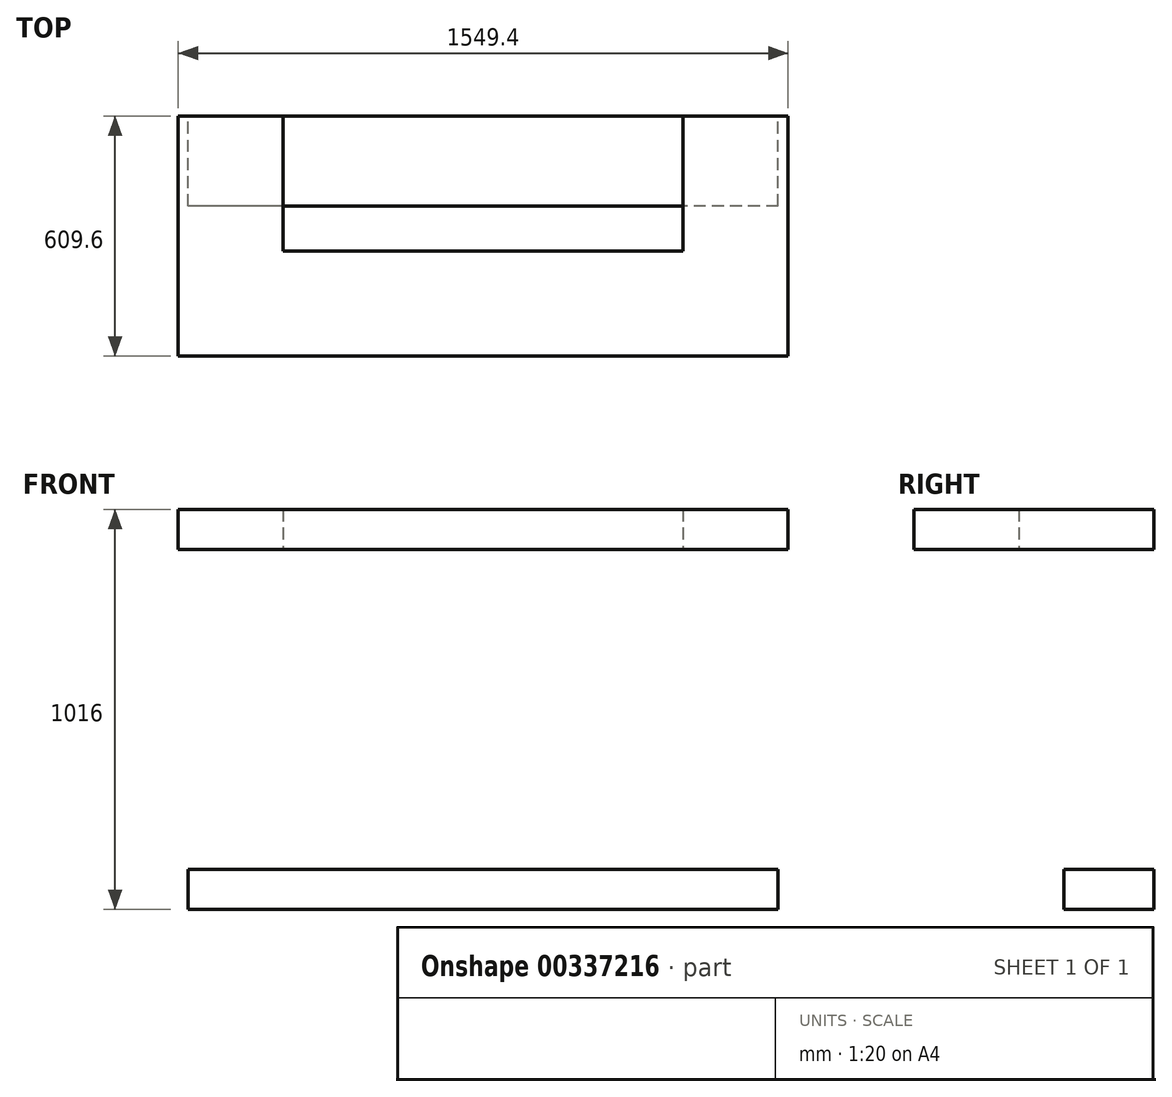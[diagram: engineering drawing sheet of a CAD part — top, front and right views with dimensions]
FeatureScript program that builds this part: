
annotation { "Feature Type Name" : "Feature", "Feature Type Description" : "" }
export const myFeature = defineFeature(function(context is Context, id is Id, definition is map)
    precondition{}
    {
        {
            var Q0;
            Q0=qCreatedBy(makeId("Top.planeOp"),FACE);
            var sketch = newSketch(context, id + "F0", { "sketchPlane" : qUnion([Q0])});
            skLineSegment(sketch, "E0", {"start": v(0, 0) * mm, "end": v(-749.3, 0) * mm, "construction": true});
            skLineSegment(sketch, "E1", {"start": v(-749.3, 0) * mm, "end": v(-749.3, -228.6) * mm, "construction": true});
            skLineSegment(sketch, "E2", {"start": v(-749.3, -228.6) * mm, "end": v(749.3, -228.6) * mm, "construction": true});
            skLineSegment(sketch, "E3.bottom", {"start": v(749.3, -228.6) * mm, "end": v(-749.3, -228.6) * mm});
            skLineSegment(sketch, "E3.top", {"start": v(749.3, 0) * mm, "end": v(-749.3, 0) * mm});
            skLineSegment(sketch, "E3.left", {"start": v(749.3, -228.6) * mm, "end": v(749.3, 0) * mm});
            skLineSegment(sketch, "E3.right", {"start": v(-749.3, -228.6) * mm, "end": v(-749.3, 0) * mm});
            skSolve(sketch);
        }
        {
            var Q0;
            Q0=makeQuery(id+"F0.imprint","IMPRINT",FACE,{"disambiguationData":[TD([[makeQuery(id+"F0.imprint","IMPRINT",EDGE,{"derivedFrom":sQuery(id+"F0.wireOp",EDGE,"E3.bottom")}),-1.0]])]});
            extrude(context, id + "F1", {"entities" : qUnion([Q0]), "depth" : 101.6 * mm});
        }
        {
            var Q0;
            Q0=qCreatedBy(makeId("Top.planeOp"),FACE);
            cPlane(context, id + "F2", {"entities" : qUnion([Q0]), "cplaneType" : CPlaneType.OFFSET, "offset" : 914.4 * mm, "width" : 152.4 * mm, "height" : 152.4 * mm});
        }
        {
            var Q0;
            Q0=qCreatedBy(id+"F2.planeOp",FACE);
            var sketch = newSketch(context, id + "F3", { "sketchPlane" : qUnion([Q0])});
            skPoint(sketch, "E4.0", {"position": v(0, 0) * mm});
            skLineSegment(sketch, "E5", {"start": v(0, 0) * mm, "end": v(-774.7, 0) * mm, "construction": true});
            skLineSegment(sketch, "E6", {"start": v(-774.7, 0) * mm, "end": v(-774.7, -609.6) * mm, "construction": true});
            skLineSegment(sketch, "E7", {"start": v(-774.7, -609.6) * mm, "end": v(774.7, -609.6) * mm, "construction": true});
            skLineSegment(sketch, "E8", {"start": v(0, 0) * mm, "end": v(508, 0) * mm, "construction": true});
            skLineSegment(sketch, "E9", {"start": v(508, 0) * mm, "end": v(508, -342.9) * mm, "construction": true});
            skLineSegment(sketch, "E10", {"start": v(508, -342.9) * mm, "end": v(-508, -342.9) * mm, "construction": true});
            skLineSegment(sketch, "E11.bottom", {"start": v(-508, -342.9) * mm, "end": v(508, -342.9) * mm, "construction": true});
            skLineSegment(sketch, "E11.top", {"start": v(-508, 0) * mm, "end": v(508, 0) * mm, "construction": true});
            skLineSegment(sketch, "E11.left", {"start": v(-508, -342.9) * mm, "end": v(-508, 0) * mm, "construction": true});
            skLineSegment(sketch, "E11.right", {"start": v(508, -342.9) * mm, "end": v(508, 0) * mm, "construction": true});
            skLineSegment(sketch, "E12.bottom", {"start": v(774.7, -609.6) * mm, "end": v(-774.7, -609.6) * mm, "construction": true});
            skLineSegment(sketch, "E12.top", {"start": v(774.7, 0) * mm, "end": v(-774.7, 0) * mm, "construction": true});
            skLineSegment(sketch, "E12.left", {"start": v(774.7, -609.6) * mm, "end": v(774.7, 0) * mm, "construction": true});
            skLineSegment(sketch, "E12.right", {"start": v(-774.7, -609.6) * mm, "end": v(-774.7, 0) * mm, "construction": true});
            skLineSegment(sketch, "E13", {"start": v(-508, 0) * mm, "end": v(-774.7, 0) * mm});
            skLineSegment(sketch, "E14", {"start": v(-774.7, -609.6) * mm, "end": v(774.7, -609.6) * mm});
            skLineSegment(sketch, "E15", {"start": v(774.7, 0) * mm, "end": v(508, 0) * mm});
            skLineSegment(sketch, "E16", {"start": v(508, -342.9) * mm, "end": v(-508, -342.9) * mm});
            skLineSegment(sketch, "E17", {"start": v(-508, -342.9) * mm, "end": v(-508, 0) * mm});
            skLineSegment(sketch, "E18", {"start": v(-774.7, 0) * mm, "end": v(-774.7, -609.6) * mm});
            skLineSegment(sketch, "E19", {"start": v(774.7, 0) * mm, "end": v(774.7, -609.6) * mm});
            skLineSegment(sketch, "E20", {"start": v(508, 0) * mm, "end": v(508, -342.9) * mm});
            skSolve(sketch);
        }
        {
            var Q0;
            Q0=makeQuery(id+"F3.imprint","IMPRINT",FACE,{"disambiguationData":[TD([[makeQuery(id+"F3.imprint","IMPRINT",EDGE,{"derivedFrom":sQuery(id+"F3.wireOp",EDGE,"E13")}),1.0]])]});
            extrude(context, id + "F4", {"entities" : qUnion([Q0]), "depth" : 101.6 * mm});
        }
    });
